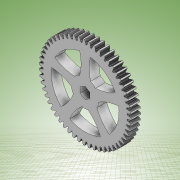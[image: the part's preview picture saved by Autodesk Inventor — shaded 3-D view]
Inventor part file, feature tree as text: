
AUTODESK INVENTOR PART (.ipt)
format: ipt  version: 2022 (Build 260153000, 153)  size: 2,796,544 bytes
history: native  units: mm
features: extrude x1, sketch x1
ambient origin geometry x8: Origin, YZ Plane, XZ Plane, XY Plane, X Axis, Y Axis, Z Axis, Center Point
bodies: Body1 (feature_tree)
feature tree (2):
  extrude  "Extrusión3"  Depth=6.0mm
  sketch  "Boceto4"  dims[d3=6.0mm d6=12.0mm d7=42.0mm d10=25.0mm d11=25.0mm d12=5.0mm d13=50.0mm d15=360.0deg d17=8.5mm d18=21.0mm d19=6.0mm d20=0.0mm]
